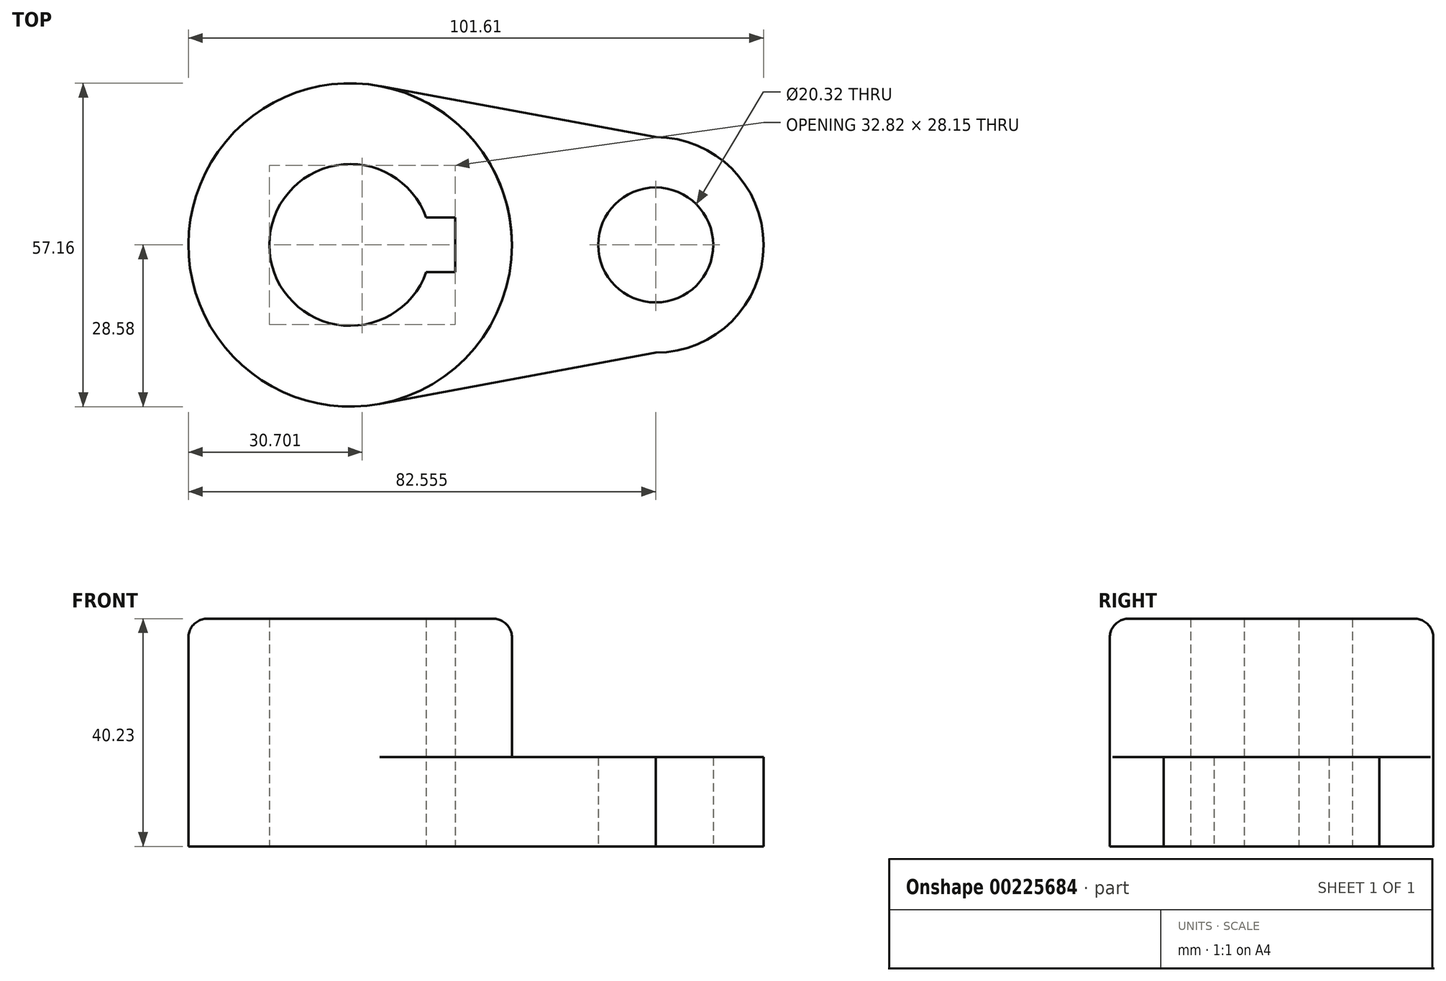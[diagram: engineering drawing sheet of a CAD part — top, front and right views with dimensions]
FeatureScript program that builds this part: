
annotation { "Feature Type Name" : "Feature", "Feature Type Description" : "" }
export const myFeature = defineFeature(function(context is Context, id is Id, definition is map)
    precondition{}
    {
        {
            var Q0;
            Q0=qCreatedBy(makeId("Top.planeOp"),FACE);
            var sketch = newSketch(context, id + "F0", { "sketchPlane" : qUnion([Q0])});
            skCircle(sketch, "E0", {"center": v(0, 0) * mm, "radius": 14.29 * mm});
            skCircle(sketch, "E1", {"center": v(0, 0) * mm, "radius": 28.58 * mm});
            skCircle(sketch, "E2", {"center": v(53.98, 0) * mm, "radius": 10.16 * mm});
            skArc(sketch, "E3", {"start": v(73.03, 0) * mm, "mid": v(67.45, -13.47) * mm, "end": v(53.98, -19.05) * mm});
            skArc(sketch, "E4", {"start": v(73.03, 0) * mm, "mid": v(67.45, 13.47) * mm, "end": v(53.98, 19.05) * mm});
            skLineSegment(sketch, "E5.bottom", {"start": v(18.53, -4.83) * mm, "end": v(-18.53, -4.83) * mm});
            skLineSegment(sketch, "E5.top", {"start": v(18.53, 4.83) * mm, "end": v(-18.53, 4.83) * mm});
            skLineSegment(sketch, "E5.left", {"start": v(18.53, -4.83) * mm, "end": v(18.53, 4.83) * mm});
            skLineSegment(sketch, "E5.right", {"start": v(-18.53, -4.83) * mm, "end": v(-18.53, 4.83) * mm});
            skLineSegment(sketch, "E6", {"start": v(53.98, -19.05) * mm, "end": v(0, -29.06) * mm});
            skLineSegment(sketch, "E7", {"start": v(53.98, 19.05) * mm, "end": v(-2.47, 29.52) * mm});
            skSolve(sketch);
        }
        {
            var Q0;
            {var subQ4=sQuery(id+"F0.wireOp",EDGE,"E5.left");Q0=makeQuery(id+"F0.imprint","IMPRINT",FACE,{"disambiguationData":[TD([[makeQuery(id+"F0.imprint","IMPRINT",EDGE,{"derivedFrom":subQ4}),-1.0]])]});}
            var Q1;
            {var subQ5=sQuery(id+"F0.wireOp",EDGE,"E5.right");Q1=makeQuery(id+"F0.imprint","IMPRINT",FACE,{"disambiguationData":[TD([[makeQuery(id+"F0.imprint","IMPRINT",EDGE,{"derivedFrom":subQ5}),-1.0]])]});}
            extrude(context, id + "F1", {"entities" : qUnion([Q0, Q1]), "depth" : 40.23 * mm});
        }
        {
            var Q0;
            Q0=makeQuery(id+"F0.imprint","IMPRINT",FACE,{"disambiguationData":[TD([[makeQuery(id+"F0.imprint","IMPRINT",EDGE,{"derivedFrom":sQuery(id+"F0.wireOp",EDGE,"E2")}),-1.0]])]});
            extrude(context, id + "F2", {"entities" : qUnion([Q0]), "operationType" : NewBodyOperationType.ADD, "depth" : 15.77 * mm});
        }
        {
            var Q0;
            Q0=makeQuery(id+"F1.opExtrude","CAP_EDGE",EDGE,{"disambiguationData":[OSD([sQuery(id+"F0.wireOp",EDGE,"E1")])],"isStart":false});
            fillet(context, id + "F3", {"entities" : qUnion([Q0]), "radius" : 3.3 * mm, "tangentPropagation" : true, "allowEdgeOverflow" : false});
        }
    });
